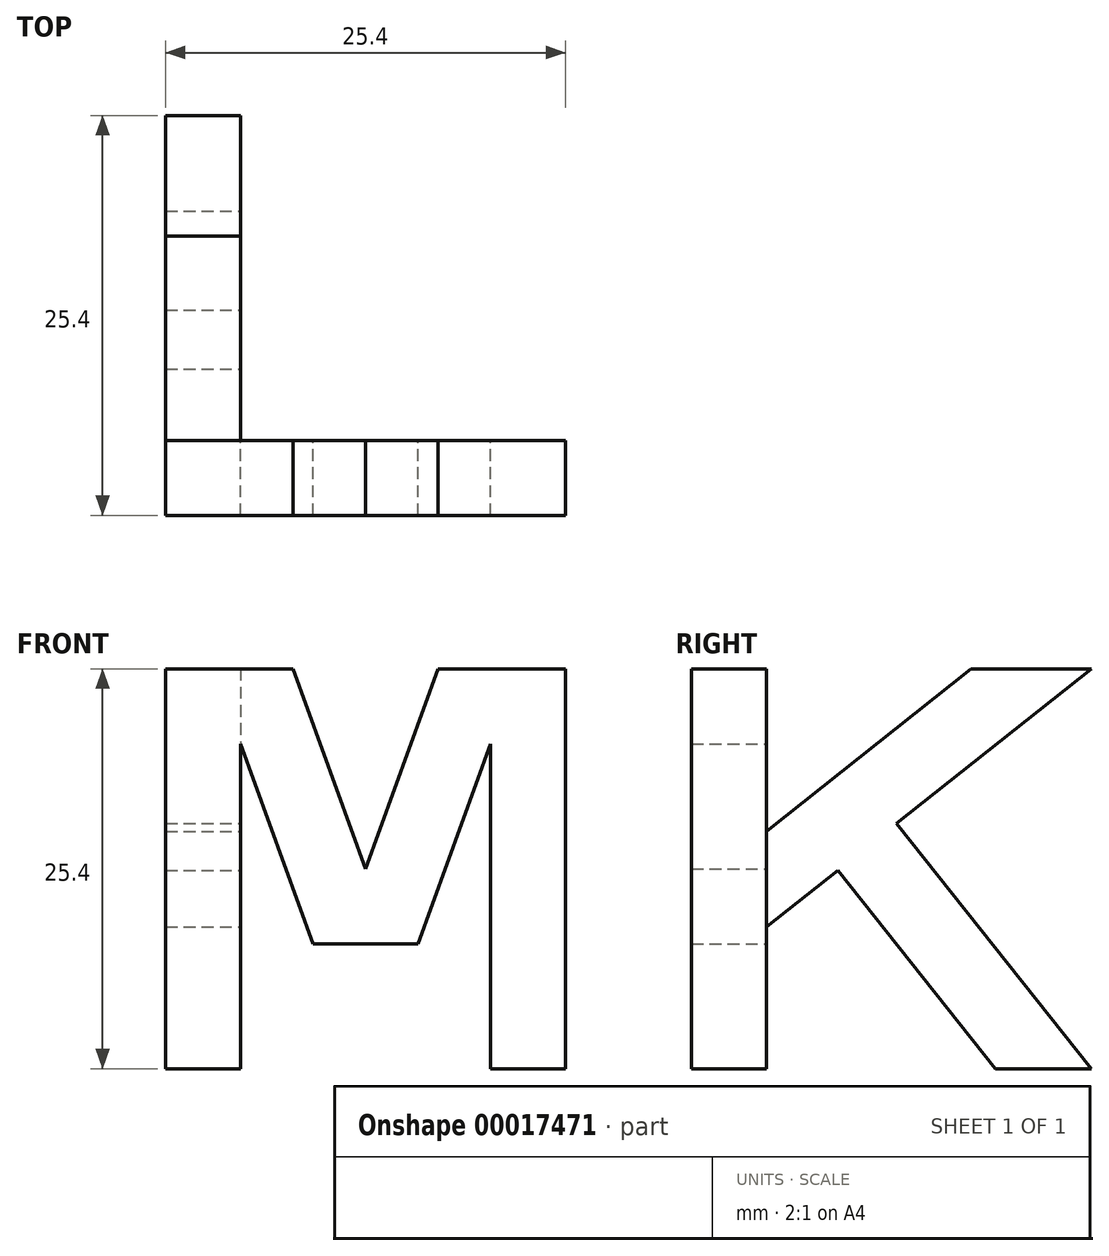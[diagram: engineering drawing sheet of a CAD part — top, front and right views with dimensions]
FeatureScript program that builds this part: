
annotation { "Feature Type Name" : "Feature", "Feature Type Description" : "" }
export const myFeature = defineFeature(function(context is Context, id is Id, definition is map)
    precondition{}
    {
        {
            var Q0;
            Q0=qCreatedBy(makeId("Front.planeOp"),FACE);
            var sketch = newSketch(context, id + "F0", { "sketchPlane" : qUnion([Q0])});
            skLineSegment(sketch, "E0", {"start": v(0, 0) * mm, "end": v(-4.6, 12.7) * mm});
            skLineSegment(sketch, "E1", {"start": v(-4.6, 12.7) * mm, "end": v(-12.7, 12.7) * mm});
            skLineSegment(sketch, "E2", {"start": v(-12.7, 12.7) * mm, "end": v(-12.7, -12.7) * mm});
            skLineSegment(sketch, "E3", {"start": v(-12.7, -12.7) * mm, "end": v(-7.94, -12.7) * mm});
            skLineSegment(sketch, "E4", {"start": v(-7.94, -12.7) * mm, "end": v(-7.94, 7.94) * mm});
            skLineSegment(sketch, "E5", {"start": v(-7.94, 7.94) * mm, "end": v(-3.34, -4.76) * mm});
            skLineSegment(sketch, "E6", {"start": v(-3.34, -4.76) * mm, "end": v(0, -4.76) * mm});
            skLineSegment(sketch, "E7", {"start": v(0, -4.76) * mm, "end": v(0, 0) * mm, "construction": true});
            skLineSegment(sketch, "E8.MirrorCS", {"start": v(0, 0) * mm, "end": v(4.6, 12.7) * mm});
            skLineSegment(sketch, "E9.MirrorCS", {"start": v(4.6, 12.7) * mm, "end": v(12.7, 12.7) * mm});
            skLineSegment(sketch, "E10.MirrorCS", {"start": v(12.7, 12.7) * mm, "end": v(12.7, -12.7) * mm});
            skLineSegment(sketch, "E11.MirrorCS", {"start": v(12.7, -12.7) * mm, "end": v(7.94, -12.7) * mm});
            skLineSegment(sketch, "E12.MirrorCS", {"start": v(7.94, -12.7) * mm, "end": v(7.94, 7.94) * mm});
            skLineSegment(sketch, "E13.MirrorCS", {"start": v(7.94, 7.94) * mm, "end": v(3.34, -4.76) * mm});
            skLineSegment(sketch, "E14.MirrorCS", {"start": v(3.34, -4.76) * mm, "end": v(0, -4.76) * mm});
            skSolve(sketch);
        }
        {
            var Q0;
            Q0 = qSketchRegion(id + "F0", true);
            extrude(context, id + "F1", {"entities" : qUnion([Q0]), "endBound" : BoundingType.SYMMETRIC, "depth" : 25.4 * mm});
        }
        {
            var Q0;
            Q0=makeQuery(id+"F1.opExtrude","SWEPT_FACE",FACE,{"disambiguationData":[OSD([sQuery(id+"F0.wireOp",EDGE,"E10.MirrorCS")])]});
            var sketch = newSketch(context, id + "F2", { "sketchPlane" : qUnion([Q0])});
            skLineSegment(sketch, "E15", {"start": v(-7.94, 12.7) * mm, "end": v(-7.94, 2.38) * mm});
            skLineSegment(sketch, "E16", {"start": v(-7.94, 2.38) * mm, "end": v(5.05, 12.7) * mm});
            skLineSegment(sketch, "E17", {"start": v(5.05, 12.7) * mm, "end": v(-7.94, 12.7) * mm});
            skLineSegment(sketch, "E18", {"start": v(12.7, 12.7) * mm, "end": v(0.33, 2.87) * mm});
            skLineSegment(sketch, "E19", {"start": v(0.33, 2.87) * mm, "end": v(12.7, -12.7) * mm});
            skLineSegment(sketch, "E20", {"start": v(12.7, -12.7) * mm, "end": v(12.7, 12.7) * mm});
            skLineSegment(sketch, "E21", {"start": v(6.62, -12.7) * mm, "end": v(-3.4, -0.1) * mm});
            skLineSegment(sketch, "E22", {"start": v(-3.4, -0.1) * mm, "end": v(-7.94, -3.7) * mm});
            skLineSegment(sketch, "E23", {"start": v(-7.94, -3.7) * mm, "end": v(-7.94, -12.7) * mm});
            skLineSegment(sketch, "E24", {"start": v(-7.94, -12.7) * mm, "end": v(6.62, -12.7) * mm});
            skSolve(sketch);
        }
        {
            var Q0;
            Q0 = qSketchRegion(id + "F2", true);
            extrude(context, id + "F3", {"entities" : qUnion([Q0]), "operationType" : NewBodyOperationType.REMOVE, "endBound" : BoundingType.THROUGH_ALL, "oppositeDirection" : true, "depth" : 25.4 * mm});
        }
        {
            var Q0;
            Q0=qCreatedBy(makeId("Top.planeOp"),FACE);
            var sketch = newSketch(context, id + "F4", { "sketchPlane" : qUnion([Q0])});
            skLineSegment(sketch, "E25.bottom", {"start": v(12.7, 12.7) * mm, "end": v(-7.94, 12.7) * mm});
            skLineSegment(sketch, "E25.top", {"start": v(12.7, -7.94) * mm, "end": v(-7.94, -7.94) * mm});
            skLineSegment(sketch, "E25.left", {"start": v(12.7, 12.7) * mm, "end": v(12.7, -7.94) * mm});
            skLineSegment(sketch, "E25.right", {"start": v(-7.94, 12.7) * mm, "end": v(-7.94, -7.94) * mm});
            skSolve(sketch);
        }
        {
            var Q0;
            Q0 = qSketchRegion(id + "F4", true);
            extrude(context, id + "F5", {"entities" : qUnion([Q0]), "operationType" : NewBodyOperationType.REMOVE, "endBound" : BoundingType.SYMMETRIC, "oppositeDirection" : true, "depth" : 25.4 * mm});
        }
    });
